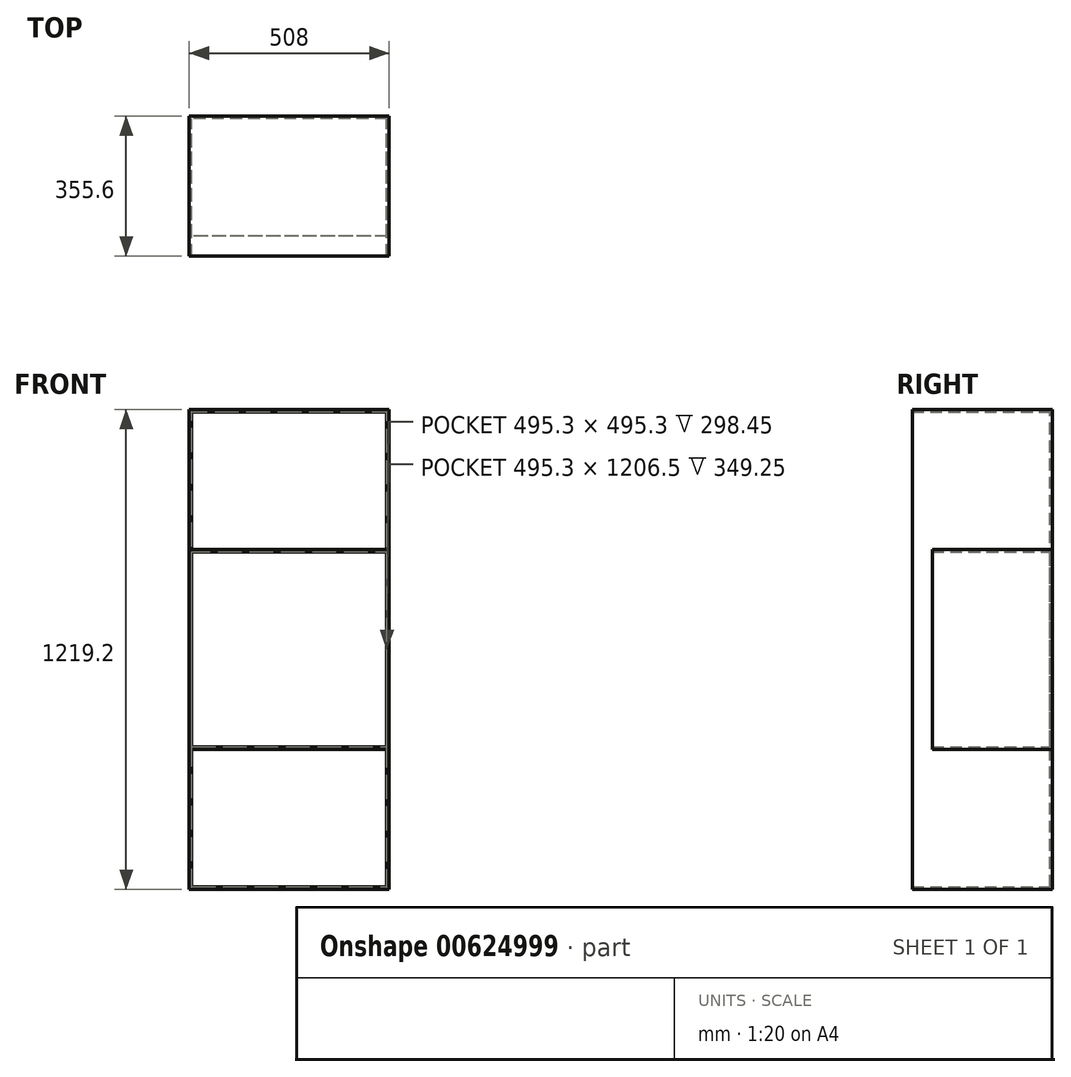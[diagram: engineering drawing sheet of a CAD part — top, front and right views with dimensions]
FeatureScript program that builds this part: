
annotation { "Feature Type Name" : "Feature", "Feature Type Description" : "" }
export const myFeature = defineFeature(function(context is Context, id is Id, definition is map)
    precondition{}
    {
        {
            var Q0;
            Q0=qCreatedBy(makeId("Front.planeOp"),FACE);
            var sketch = newSketch(context, id + "F0", { "sketchPlane" : qUnion([Q0])});
            skLineSegment(sketch, "E0.bottom", {"start": v(254, -609.6) * mm, "end": v(-254, -609.6) * mm});
            skLineSegment(sketch, "E0.top", {"start": v(254, 609.6) * mm, "end": v(-254, 609.6) * mm});
            skLineSegment(sketch, "E0.left", {"start": v(254, -609.6) * mm, "end": v(254, 609.6) * mm});
            skLineSegment(sketch, "E0.right", {"start": v(-254, -609.6) * mm, "end": v(-254, 609.6) * mm});
            skPoint(sketch, "E0.middle", {"position": v(0, 0) * mm});
            skSolve(sketch);
        }
        {
            var Q0;
            Q0 = qSketchRegion(id + "F0", true);
            extrude(context, id + "F1", {"entities" : qUnion([Q0]), "depth" : 355.6 * mm, "offsetDistance" : 25 * mm});
        }
        {
            var Q0;
            Q0=qCreatedBy(makeId("Front.planeOp"),FACE);
            var sketch = newSketch(context, id + "F2", { "sketchPlane" : qUnion([Q0])});
            skLineSegment(sketch, "E1.bottom", {"start": v(254, -254) * mm, "end": v(-254, -254) * mm});
            skLineSegment(sketch, "E1.top", {"start": v(254, 254) * mm, "end": v(-254, 254) * mm});
            skLineSegment(sketch, "E1.left", {"start": v(254, -254) * mm, "end": v(254, 254) * mm});
            skLineSegment(sketch, "E1.right", {"start": v(-254, -254) * mm, "end": v(-254, 254) * mm});
            skPoint(sketch, "E1.middle", {"position": v(0, 0) * mm});
            skSolve(sketch);
        }
        {
            var Q0;
            Q0 = qSketchRegion(id + "F2", true);
            extrude(context, id + "F3", {"entities" : qUnion([Q0]), "depth" : 304.8 * mm, "offsetDistance" : 25 * mm});
        }
        {
            var Q0;
            Q0=makeQuery(id+"F3.opExtrude","CAP_FACE",FACE,{"disambiguationData":[OSD([sQuery(id+"F2.wireOp",EDGE,"E1.bottom"),sQuery(id+"F2.wireOp",EDGE,"E1.top"),sQuery(id+"F2.wireOp",EDGE,"E1.left"),sQuery(id+"F2.wireOp",EDGE,"E1.right")])],"isStart":false});
            shell(context, id + "F4", {"entities" : qUnion([Q0]), "thickness" : 6.35 * mm});
        }
        {
            var Q0;
            Q0=makeQuery(id+"F1.opExtrude","CAP_FACE",FACE,{"disambiguationData":[OSD([sQuery(id+"F0.wireOp",EDGE,"E0.bottom"),sQuery(id+"F0.wireOp",EDGE,"E0.top"),sQuery(id+"F0.wireOp",EDGE,"E0.left"),sQuery(id+"F0.wireOp",EDGE,"E0.right")])],"isStart":false});
            shell(context, id + "F5", {"entities" : qUnion([Q0]), "thickness" : 6.35 * mm});
        }
    });
